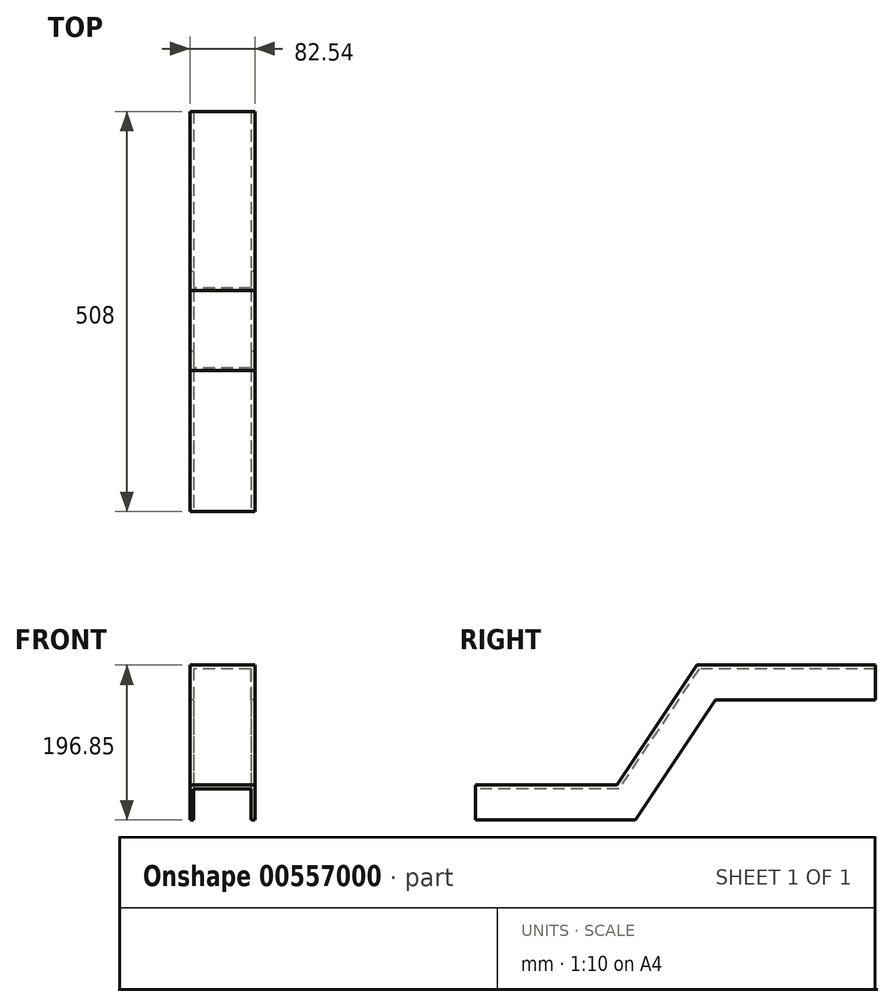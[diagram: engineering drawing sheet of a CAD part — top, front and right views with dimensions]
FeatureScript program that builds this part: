
annotation { "Feature Type Name" : "Feature", "Feature Type Description" : "" }
export const myFeature = defineFeature(function(context is Context, id is Id, definition is map)
    precondition{}
    {
        {
            var Q0;
            Q0=qCreatedBy(makeId("Front.planeOp"),FACE);
            var sketch = newSketch(context, id + "F0", { "sketchPlane" : qUnion([Q0])});
            skLineSegment(sketch, "E0", {"start": v(-41.28, 0) * mm, "end": v(-41.28, 44.45) * mm});
            skLineSegment(sketch, "E1", {"start": v(-41.28, 44.45) * mm, "end": v(41.27, 44.45) * mm});
            skLineSegment(sketch, "E2", {"start": v(41.27, 44.45) * mm, "end": v(41.27, 0) * mm});
            skLineSegment(sketch, "E3", {"start": v(41.27, 0) * mm, "end": v(36.51, 0) * mm});
            skLineSegment(sketch, "E4", {"start": v(36.51, 0) * mm, "end": v(36.51, 39.69) * mm});
            skLineSegment(sketch, "E5", {"start": v(36.51, 39.69) * mm, "end": v(-36.51, 39.69) * mm});
            skLineSegment(sketch, "E6", {"start": v(-36.51, 39.69) * mm, "end": v(-36.51, 0) * mm});
            skLineSegment(sketch, "E7", {"start": v(-36.51, 0) * mm, "end": v(-41.28, 0) * mm});
            skSolve(sketch);
        }
        {
            var Q0;
            Q0=qCreatedBy(makeId("Right.planeOp"),FACE);
            var sketch = newSketch(context, id + "F1", { "sketchPlane" : qUnion([Q0])});
            skLineSegment(sketch, "E8", {"start": v(0, 0) * mm, "end": v(-203.2, 0) * mm});
            skLineSegment(sketch, "E9", {"start": v(-203.2, 0) * mm, "end": v(-304.8, -152.4) * mm});
            skLineSegment(sketch, "E10", {"start": v(-304.8, -152.4) * mm, "end": v(-508, -152.4) * mm});
            skSolve(sketch);
        }
        {
            var Q0;
            Q0=makeQuery(id+"F0.imprint","IMPRINT",FACE,{"disambiguationData":[TD([[makeQuery(id+"F0.imprint","IMPRINT",EDGE,{"derivedFrom":sQuery(id+"F0.wireOp",EDGE,"E0")}),-1.0]])]});
            var Q1;
            Q1=sQuery(id+"F1.wireOp",EDGE,"E8");
            var Q2;
            Q2=sQuery(id+"F1.wireOp",EDGE,"E9");
            var Q3;
            Q3=sQuery(id+"F1.wireOp",EDGE,"E10");
            sweep(context, id + "F2", {"profiles" : qUnion([Q0]), "path" : qUnion([Q1, Q2, Q3])});
        }
    });
